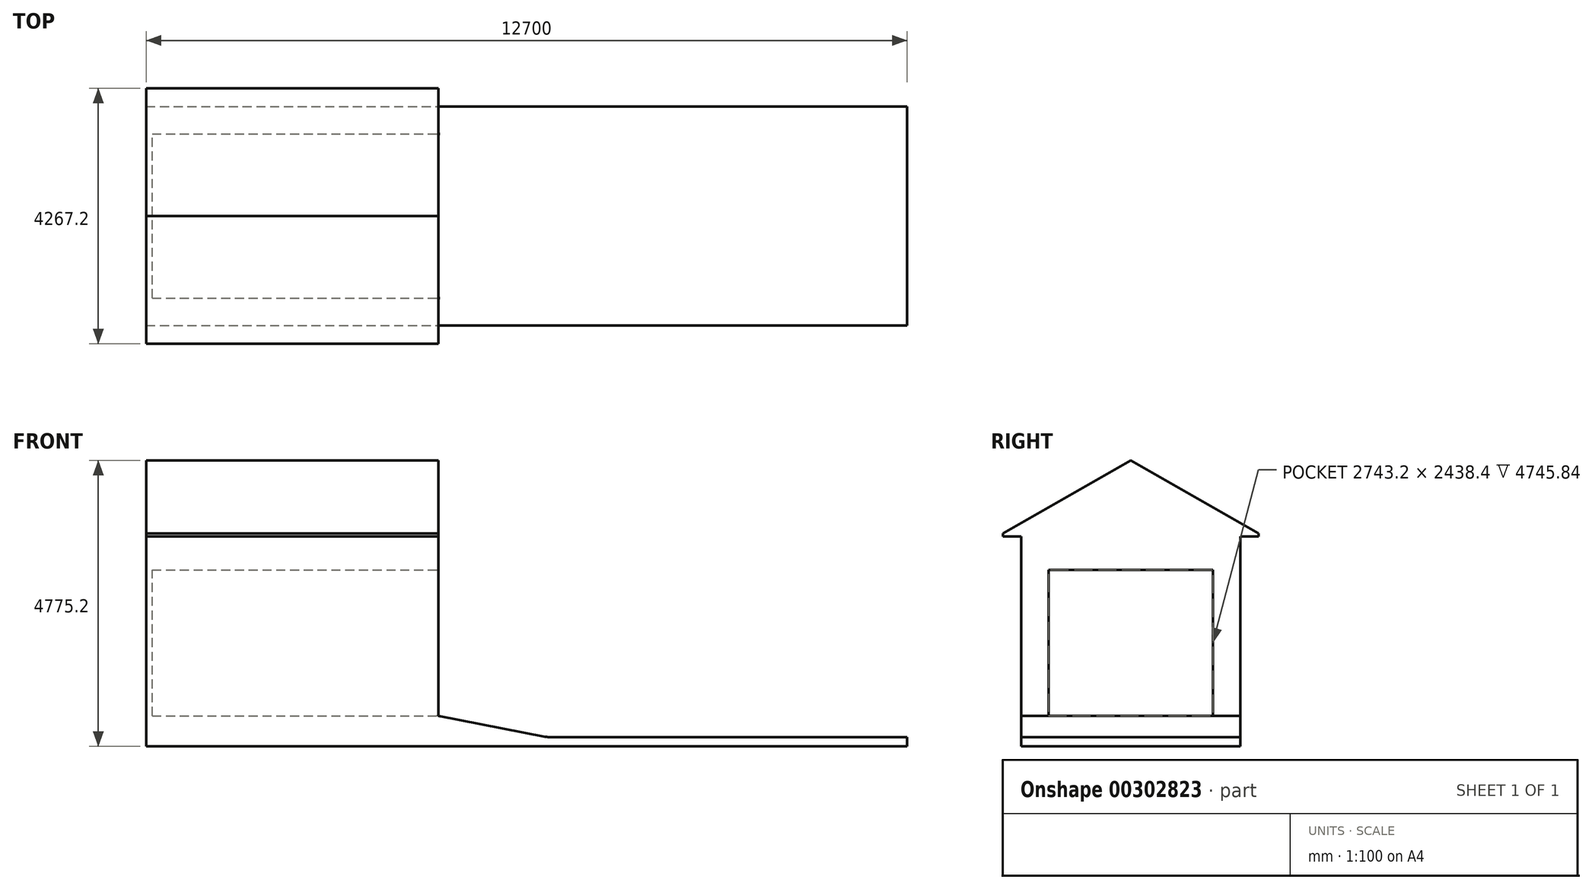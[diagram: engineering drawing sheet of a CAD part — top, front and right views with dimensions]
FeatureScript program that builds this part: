
annotation { "Feature Type Name" : "Feature", "Feature Type Description" : "" }
export const myFeature = defineFeature(function(context is Context, id is Id, definition is map)
    precondition{}
    {
        {
            var Q0;
            Q0=qCreatedBy(makeId("Front.planeOp"),FACE);
            var sketch = newSketch(context, id + "F0", { "sketchPlane" : qUnion([Q0])});
            skLineSegment(sketch, "E0.bottom", {"start": v(-4876.8, 3403.6) * mm, "end": v(0, 3403.6) * mm});
            skLineSegment(sketch, "E0.top", {"start": v(-4876.8, 355.6) * mm, "end": v(0, 355.6) * mm});
            skLineSegment(sketch, "E0.left", {"start": v(-4876.8, 3403.6) * mm, "end": v(-4876.8, 355.6) * mm});
            skLineSegment(sketch, "E0.right", {"start": v(0, 3403.6) * mm, "end": v(0, 355.6) * mm});
            skSolve(sketch);
        }
        {
            var Q0;
            Q0 = qSketchRegion(id + "F0", true);
            extrude(context, id + "F1", {"entities" : qUnion([Q0]), "oppositeDirection" : true, "depth" : 3657.6 * mm, "symmetric" : true});
        }
        {
            var Q0;
            Q0=qCreatedBy(makeId("Right.planeOp"),FACE);
            var sketch = newSketch(context, id + "F2", { "sketchPlane" : qUnion([Q0])});
            skLineSegment(sketch, "E1", {"start": v(-1828.8, 3352.8) * mm, "end": v(-2133.6, 3352.8) * mm});
            skLineSegment(sketch, "E2", {"start": v(-2133.6, 3352.8) * mm, "end": v(-2133.6, 3403.6) * mm});
            skLineSegment(sketch, "E3", {"start": v(-2133.6, 3403.6) * mm, "end": v(0, 4622.8) * mm});
            skLineSegment(sketch, "E4.MirrorCS", {"start": v(2133.6, 3403.6) * mm, "end": v(0, 4622.8) * mm});
            skLineSegment(sketch, "E5.MirrorCS", {"start": v(2133.6, 3352.8) * mm, "end": v(2133.6, 3403.6) * mm});
            skLineSegment(sketch, "E6.MirrorCS", {"start": v(1828.8, 3352.8) * mm, "end": v(2133.6, 3352.8) * mm});
            skLineSegment(sketch, "E7.0", {"start": v(1828.8, 3403.6) * mm, "end": v(-1828.8, 3403.6) * mm});
            skLineSegment(sketch, "E8", {"start": v(-1828.8, 3403.6) * mm, "end": v(-1828.8, 3352.8) * mm});
            skLineSegment(sketch, "E9", {"start": v(1828.8, 3403.6) * mm, "end": v(1828.8, 3352.8) * mm});
            skSolve(sketch);
        }
        {
            var Q0;
            Q0 = qSketchRegion(id + "F2", true);
            var Q1;
            Q1=makeQuery(id+"F1.opExtrude","SWEPT_FACE",FACE,{"disambiguationData":[OSD([sQuery(id+"F0.wireOp",EDGE,"E0.left")])]});
            extrude(context, id + "F3", {"entities" : qUnion([Q0]), "operationType" : NewBodyOperationType.ADD, "endBound" : BoundingType.UP_TO_SURFACE, "oppositeDirection" : true, "endBoundEntityFace" : qUnion([Q1]), "depth" : 25.4 * mm});
        }
        {
            var Q0;
            Q0=qCreatedBy(makeId("Front.planeOp"),FACE);
            var sketch = newSketch(context, id + "F4", { "sketchPlane" : qUnion([Q0])});
            skLineSegment(sketch, "E10", {"start": v(-4876.8, 0) * mm, "end": v(1828.8, 0) * mm});
            skLineSegment(sketch, "E11", {"start": v(1828.8, 0) * mm, "end": v(0, 355.6) * mm});
            skLineSegment(sketch, "E12", {"start": v(-4876.8, 0) * mm, "end": v(-4876.8, 355.6) * mm});
            skLineSegment(sketch, "E13", {"start": v(-4876.8, 355.6) * mm, "end": v(0, 355.6) * mm});
            skSolve(sketch);
        }
        {
            var Q0;
            Q0=makeQuery(id+"F4.imprint","IMPRINT",FACE,{"disambiguationData":[TD([[makeQuery(id+"F4.imprint","IMPRINT",EDGE,{"derivedFrom":sQuery(id+"F4.wireOp",EDGE,"E10")}),1.0]])]});
            extrude(context, id + "F5", {"entities" : qUnion([Q0]), "operationType" : NewBodyOperationType.ADD, "oppositeDirection" : true, "depth" : 2743.2 * mm, "symmetric" : true});
        }
        {
            var Q0;
            Q0=qCreatedBy(makeId("Front.planeOp"),FACE);
            var sketch = newSketch(context, id + "F6", { "sketchPlane" : qUnion([Q0])});
            skLineSegment(sketch, "E14.0.0", {"start": v(0, 355.6) * mm, "end": v(-4876.8, 355.6) * mm});
            skLineSegment(sketch, "E14.0.1", {"start": v(-4876.8, 355.6) * mm, "end": v(-4876.8, 0) * mm});
            skLineSegment(sketch, "E14.0.2", {"start": v(-4876.8, 0) * mm, "end": v(1828.8, 0) * mm});
            skLineSegment(sketch, "E14.0.3", {"start": v(1828.8, 0) * mm, "end": v(0, 355.6) * mm});
            skLineSegment(sketch, "E15.bottom", {"start": v(-4876.8, 0) * mm, "end": v(7823.2, 0) * mm});
            skLineSegment(sketch, "E15.top", {"start": v(-4876.8, -152.4) * mm, "end": v(7823.2, -152.4) * mm});
            skLineSegment(sketch, "E15.left", {"start": v(-4876.8, 0) * mm, "end": v(-4876.8, -152.4) * mm});
            skLineSegment(sketch, "E15.right", {"start": v(7823.2, 0) * mm, "end": v(7823.2, -152.4) * mm});
            skSolve(sketch);
        }
        {
            var Q0;
            Q0 = qSketchRegion(id + "F6", true);
            extrude(context, id + "F7", {"entities" : qUnion([Q0]), "operationType" : NewBodyOperationType.ADD, "depth" : 2743.2 * mm, "symmetric" : true});
        }
        {
            var Q0;
            Q0=makeQuery(id+"F7.boolean.opBoolean","MERGE",EDGE,{"derivedFrom":[makeQuery(id+"F5.opExtrude","SWEPT_EDGE",EDGE,{"disambiguationData":[OSD([sQuery(id+"F4.wireOp",EDGE,"E10"),sQuery(id+"F4.wireOp",EDGE,"E11")])]}),makeQuery(id+"F7.opExtrude","SWEPT_EDGE",EDGE,{"disambiguationData":[OSD([sQuery(id+"F6.wireOp",EDGE,"E14.0.3"),sQuery(id+"F6.wireOp",EDGE,"E15.bottom")])]})]});
            fillet(context, id + "F8", {"entities" : qUnion([Q0]), "radius" : 508 * mm, "tangentPropagation" : true, "allowEdgeOverflow" : false});
        }
        {
            var Q0;
            Q0=qCreatedBy(makeId("Right.planeOp"),FACE);
            var sketch = newSketch(context, id + "F9", { "sketchPlane" : qUnion([Q0])});
            skLineSegment(sketch, "E16.bottom", {"start": v(-1371.6, 355.6) * mm, "end": v(1371.6, 355.6) * mm});
            skLineSegment(sketch, "E16.top", {"start": v(-1371.6, 2794) * mm, "end": v(1371.6, 2794) * mm});
            skLineSegment(sketch, "E16.left", {"start": v(-1371.6, 355.6) * mm, "end": v(-1371.6, 2794) * mm});
            skLineSegment(sketch, "E16.right", {"start": v(1371.6, 355.6) * mm, "end": v(1371.6, 2794) * mm});
            skSolve(sketch);
        }
        {
            var Q0;
            Q0=makeQuery(id+"F7.boolean.opBoolean","MERGE",FACE,{"derivedFrom":[makeQuery(id+"F5.opExtrude","CAP_FACE",FACE,{"disambiguationData":[OSD([sQuery(id+"F4.wireOp",EDGE,"E10"),sQuery(id+"F4.wireOp",EDGE,"E11"),sQuery(id+"F4.wireOp",EDGE,"E12"),sQuery(id+"F4.wireOp",EDGE,"E13")])],"isStart":true}),makeQuery(id+"F7.opExtrude","CAP_FACE",FACE,{"disambiguationData":[OSD([sQuery(id+"F6.wireOp",EDGE,"E14.0.0"),sQuery(id+"F6.wireOp",EDGE,"E14.0.1"),sQuery(id+"F6.wireOp",EDGE,"E14.0.3"),sQuery(id+"F6.wireOp",EDGE,"E15.bottom"),sQuery(id+"F6.wireOp",EDGE,"E15.top"),sQuery(id+"F6.wireOp",EDGE,"E15.left"),sQuery(id+"F6.wireOp",EDGE,"E15.right")])],"isStart":false})]});
            extrude(context, id + "F10", {"entities" : qUnion([Q0]), "operationType" : NewBodyOperationType.ADD, "depth" : 457.2 * mm, "hasSecondDirection" : true, "secondDirectionOppositeDirection" : true, "secondDirectionDepth" : 3200.4 * mm});
        }
        {
            var Q0;
            Q0=makeQuery(id+"F9.imprint","IMPRINT",FACE,{"disambiguationData":[TD([[makeQuery(id+"F9.imprint","IMPRINT",EDGE,{"derivedFrom":sQuery(id+"F9.wireOp",EDGE,"E16.bottom")}),1.0]])]});
            extrude(context, id + "F11", {"entities" : qUnion([Q0]), "operationType" : NewBodyOperationType.REMOVE, "oppositeDirection" : true, "depth" : 4775.2 * mm});
        }
        {
            var Q0;
            {var subQ0=sQuery(id+"F4.wireOp",EDGE,"E13");var subQ1=sQuery(id+"F4.wireOp",EDGE,"E11");var subQ3=sQuery(id+"F0.wireOp",EDGE,"E0.top");var subQ5=sQuery(id+"F0.wireOp",EDGE,"E0.right");var subQ7=sQuery(id+"F0.wireOp",EDGE,"E0.left");var subQ8=sQuery(id+"F0.wireOp",EDGE,"E0.bottom");var subQ12=makeQuery(id+"F1.opExtrude","SWEPT_EDGE",EDGE,{"disambiguationData":[OSD([subQ3,subQ5])]});Q0=makeQuery(id+"F11.boolean.opBoolean","MERGE",EDGE,{"derivedFrom":[makeQuery(id+"F10.boolean.opBoolean","MERGE",EDGE,{"derivedFrom":[makeQuery(id+"F5.boolean.opBoolean","MERGE",EDGE,{"derivedFrom":[subQ12,makeQuery(id+"F5.opExtrude","SWEPT_EDGE",EDGE,{"disambiguationData":[OSD([subQ1,subQ0])]})]}),makeQuery(id+"F5.boolean.opBoolean","SPLIT",EDGE,{"disambiguationData":[TD([makeQuery(id+"F1.opExtrude","CAP_FACE",FACE,{"disambiguationData":[OSD([subQ8,subQ3,subQ7,subQ5])],"isStart":true})])],"derivedFrom":subQ12}),makeQuery(id+"F5.boolean.opBoolean","SPLIT",EDGE,{"disambiguationData":[TD([makeQuery(id+"F1.opExtrude","CAP_FACE",FACE,{"disambiguationData":[OSD([subQ8,subQ3,subQ7,subQ5])],"isStart":false})])],"derivedFrom":subQ12}),makeQuery(id+"F10.opExtrude","SWEPT_EDGE",EDGE,{"disambiguationData":[OSD([subQ1,subQ0])]})]}),makeQuery(id+"F11.opExtrude","CAP_EDGE",EDGE,{"disambiguationData":[OSD([sQuery(id+"F9.wireOp",EDGE,"E16.bottom")])],"isStart":true})]});}
            fillet(context, id + "F12", {"entities" : qUnion([Q0]), "radius" : 304.8 * mm, "tangentPropagation" : true, "allowEdgeOverflow" : false});
        }
    });
